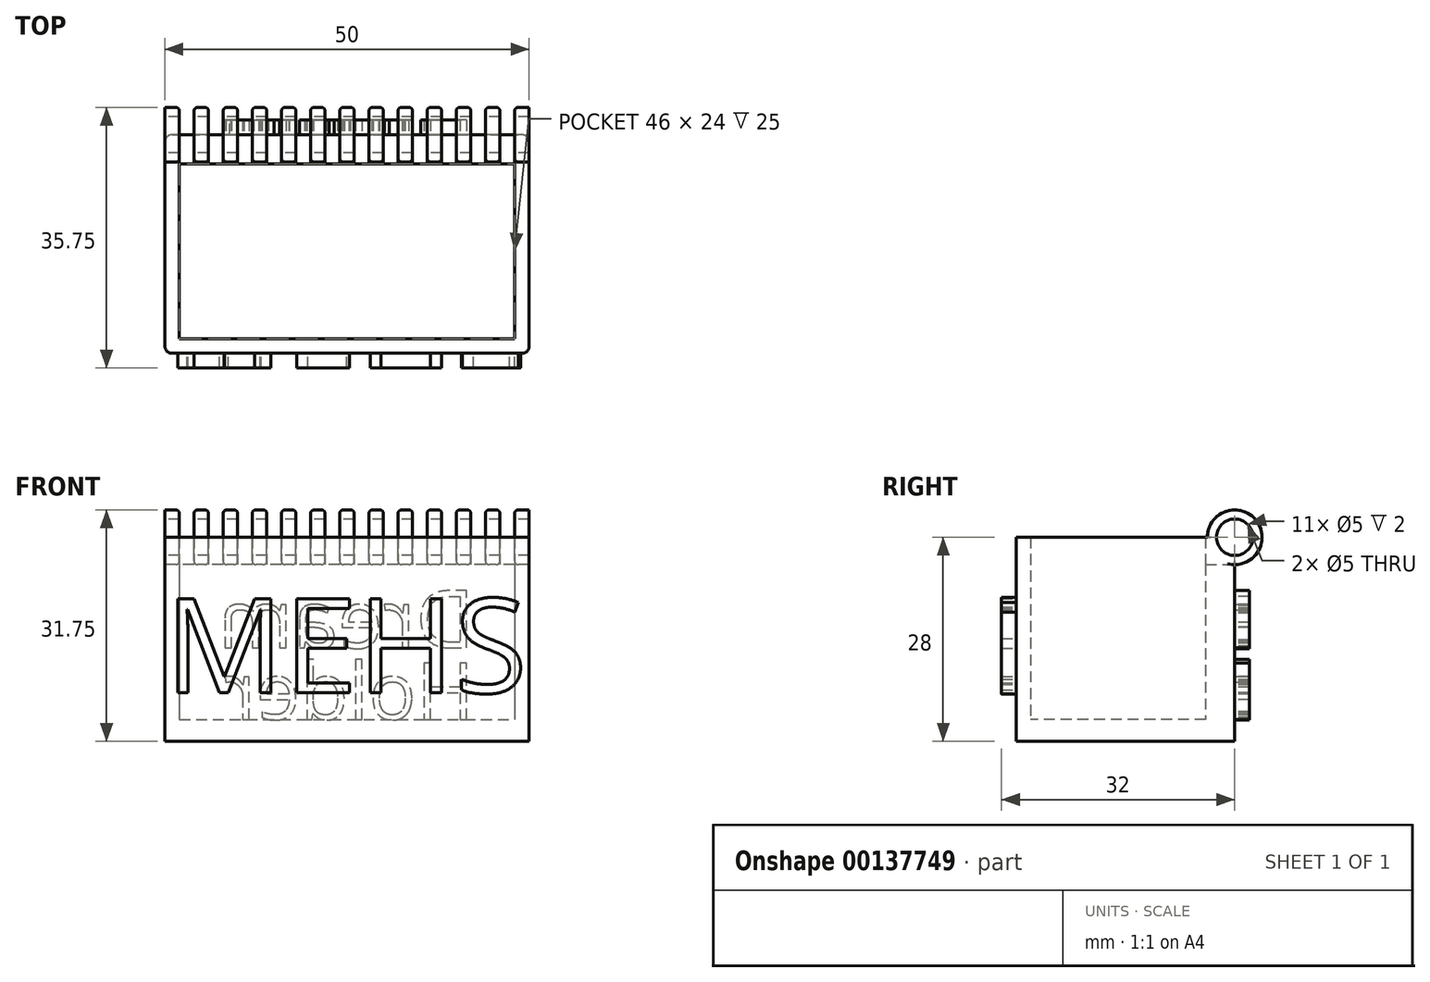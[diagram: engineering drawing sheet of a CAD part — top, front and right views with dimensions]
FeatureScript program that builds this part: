
annotation { "Feature Type Name" : "Feature", "Feature Type Description" : "" }
export const myFeature = defineFeature(function(context is Context, id is Id, definition is map)
    precondition{}
    {
        {
            var Q0;
            Q0=qCreatedBy(makeId("Top.planeOp"),FACE);
            var sketch = newSketch(context, id + "F0", { "sketchPlane" : qUnion([Q0])});
            skLineSegment(sketch, "E0.bottom", {"start": v(-25, 15) * mm, "end": v(25, 15) * mm});
            skLineSegment(sketch, "E0.top", {"start": v(-25, -15) * mm, "end": v(25, -15) * mm});
            skLineSegment(sketch, "E0.left", {"start": v(-25, 15) * mm, "end": v(-25, -15) * mm});
            skLineSegment(sketch, "E0.right", {"start": v(25, 15) * mm, "end": v(25, -15) * mm});
            skSolve(sketch);
        }
        {
            var Q0;
            Q0 = qSketchRegion(id + "F0", true);
            extrude(context, id + "F1", {"entities" : qUnion([Q0]), "depth" : 3 * mm});
        }
        {
            var Q0;
            Q0=makeQuery(id+"F1.opExtrude","CAP_FACE",FACE,{"disambiguationData":[OSD([sQuery(id+"F0.wireOp",EDGE,"E0.bottom"),sQuery(id+"F0.wireOp",EDGE,"E0.top"),sQuery(id+"F0.wireOp",EDGE,"E0.left"),sQuery(id+"F0.wireOp",EDGE,"E0.right")])],"isStart":false});
            var sketch = newSketch(context, id + "F2", { "sketchPlane" : qUnion([Q0])});
            skLineSegment(sketch, "E1.bottom", {"start": v(-25, 15) * mm, "end": v(25, 15) * mm});
            skLineSegment(sketch, "E1.top", {"start": v(-25, -15) * mm, "end": v(25, -15) * mm});
            skLineSegment(sketch, "E1.left", {"start": v(-25, 15) * mm, "end": v(-25, -15) * mm});
            skLineSegment(sketch, "E1.right", {"start": v(25, 15) * mm, "end": v(25, -15) * mm});
            skLineSegment(sketch, "E2.bottom", {"start": v(-23, 11) * mm, "end": v(23, 11) * mm});
            skLineSegment(sketch, "E2.top", {"start": v(-23, -13) * mm, "end": v(23, -13) * mm});
            skLineSegment(sketch, "E2.left", {"start": v(-23, 11) * mm, "end": v(-23, -13) * mm});
            skLineSegment(sketch, "E2.right", {"start": v(23, 11) * mm, "end": v(23, -13) * mm});
            skSolve(sketch);
        }
        {
            var Q0;
            Q0 = qSketchRegion(id + "F2", true);
            extrude(context, id + "F3", {"entities" : qUnion([Q0]), "operationType" : NewBodyOperationType.ADD, "depth" : 25 * mm});
        }
        {
            var Q0;
            Q0=makeQuery(id+"F3.boolean.opBoolean","MERGE",FACE,{"derivedFrom":[makeQuery(id+"F1.opExtrude","SWEPT_FACE",FACE,{"disambiguationData":[OSD([sQuery(id+"F0.wireOp",EDGE,"E0.left")])]}),makeQuery(id+"F3.opExtrude","SWEPT_FACE",FACE,{"disambiguationData":[OSD([sQuery(id+"F2.wireOp",EDGE,"E1.left")])]})]});
            var sketch = newSketch(context, id + "F4", { "sketchPlane" : qUnion([Q0])});
            skCircle(sketch, "E3", {"center": v(-15, 28) * mm, "radius": 2.5 * mm});
            skCircle(sketch, "E4", {"center": v(-15, 28) * mm, "radius": 3.75 * mm});
            skSolve(sketch);
        }
        {
            var Q0;
            Q0 = qSketchRegion(id + "F4", true);
            var Q1;
            Q1=makeQuery(id+"F3.boolean.opBoolean","MERGE",FACE,{"derivedFrom":[makeQuery(id+"F1.opExtrude","SWEPT_FACE",FACE,{"disambiguationData":[OSD([sQuery(id+"F0.wireOp",EDGE,"E0.right")])]}),makeQuery(id+"F3.opExtrude","SWEPT_FACE",FACE,{"disambiguationData":[OSD([sQuery(id+"F2.wireOp",EDGE,"E1.right")])]})]});
            extrude(context, id + "F5", {"entities" : qUnion([Q0]), "operationType" : NewBodyOperationType.ADD, "endBound" : BoundingType.UP_TO_SURFACE, "oppositeDirection" : true, "endBoundEntityFace" : qUnion([Q1]), "depth" : 25 * mm});
        }
        {
            var Q0;
            Q0=makeQuery(id+"F5.boolean.opBoolean","MERGE",FACE,{"derivedFrom":[makeQuery(id+"F3.boolean.opBoolean","MERGE",FACE,{"derivedFrom":[makeQuery(id+"F1.opExtrude","SWEPT_FACE",FACE,{"disambiguationData":[OSD([sQuery(id+"F0.wireOp",EDGE,"E0.right")])]}),makeQuery(id+"F3.opExtrude","SWEPT_FACE",FACE,{"disambiguationData":[OSD([sQuery(id+"F2.wireOp",EDGE,"E1.right")])]})]}),makeQuery(id+"F5.opExtrude","CAP_FACE",FACE,{"disambiguationData":[OSD([sQuery(id+"F4.wireOp",EDGE,"E3"),sQuery(id+"F4.wireOp",EDGE,"E4")])],"isStart":false})]});
            var sketch = newSketch(context, id + "F6", { "sketchPlane" : qUnion([Q0])});
            skCircle(sketch, "E5", {"center": v(15, 28) * mm, "radius": 2.5 * mm});
            skSolve(sketch);
        }
        {
            var Q0;
            Q0 = qSketchRegion(id + "F6", true);
            extrude(context, id + "F7", {"entities" : qUnion([Q0]), "operationType" : NewBodyOperationType.REMOVE, "endBound" : BoundingType.THROUGH_ALL, "oppositeDirection" : true, "depth" : 25 * mm});
        }
        {
            var Q0;
            Q0=qCreatedBy(makeId("Front.planeOp"),FACE);
            cPlane(context, id + "F8", {"entities" : qUnion([Q0]), "cplaneType" : CPlaneType.OFFSET, "offset" : 19 * mm, "oppositeDirection" : true, "width" : 150 * mm, "height" : 150 * mm});
        }
        {
            var Q0;
            Q0=qCreatedBy(id+"F8.planeOp",FACE);
            var sketch = newSketch(context, id + "F9", { "sketchPlane" : qUnion([Q0])});
            skLineSegment(sketch, "E6.bottom", {"start": v(23, 31.75) * mm, "end": v(21, 31.75) * mm});
            skLineSegment(sketch, "E6.top", {"start": v(23, 24.25) * mm, "end": v(21, 24.25) * mm});
            skLineSegment(sketch, "E6.left", {"start": v(23, 31.75) * mm, "end": v(23, 24.25) * mm});
            skLineSegment(sketch, "E6.right", {"start": v(21, 31.75) * mm, "end": v(21, 24.25) * mm});
            skLineSegment(sketch, "E7.1.0.0", {"start": v(17, 31.75) * mm, "end": v(17, 24.25) * mm});
            skLineSegment(sketch, "E7.1.0.1", {"start": v(19, 31.75) * mm, "end": v(17, 31.75) * mm});
            skLineSegment(sketch, "E7.1.0.2", {"start": v(19, 24.25) * mm, "end": v(17, 24.25) * mm});
            skLineSegment(sketch, "E7.1.0.3", {"start": v(19, 31.75) * mm, "end": v(19, 24.25) * mm});
            skLineSegment(sketch, "E7.2.0.0", {"start": v(13, 31.75) * mm, "end": v(13, 24.25) * mm});
            skLineSegment(sketch, "E7.2.0.1", {"start": v(15, 31.75) * mm, "end": v(13, 31.75) * mm});
            skLineSegment(sketch, "E7.2.0.2", {"start": v(15, 24.25) * mm, "end": v(13, 24.25) * mm});
            skLineSegment(sketch, "E7.2.0.3", {"start": v(15, 31.75) * mm, "end": v(15, 24.25) * mm});
            skLineSegment(sketch, "E7.3.0.0", {"start": v(9, 31.75) * mm, "end": v(9, 24.25) * mm});
            skLineSegment(sketch, "E7.3.0.1", {"start": v(11, 31.75) * mm, "end": v(9, 31.75) * mm});
            skLineSegment(sketch, "E7.3.0.2", {"start": v(11, 24.25) * mm, "end": v(9, 24.25) * mm});
            skLineSegment(sketch, "E7.3.0.3", {"start": v(11, 31.75) * mm, "end": v(11, 24.25) * mm});
            skLineSegment(sketch, "E7.4.0.0", {"start": v(5, 31.75) * mm, "end": v(5, 24.25) * mm});
            skLineSegment(sketch, "E7.4.0.1", {"start": v(7, 31.75) * mm, "end": v(5, 31.75) * mm});
            skLineSegment(sketch, "E7.4.0.2", {"start": v(7, 24.25) * mm, "end": v(5, 24.25) * mm});
            skLineSegment(sketch, "E7.4.0.3", {"start": v(7, 31.75) * mm, "end": v(7, 24.25) * mm});
            skLineSegment(sketch, "E7.5.0.0", {"start": v(1, 31.75) * mm, "end": v(1, 24.25) * mm});
            skLineSegment(sketch, "E7.5.0.1", {"start": v(3, 31.75) * mm, "end": v(1, 31.75) * mm});
            skLineSegment(sketch, "E7.5.0.2", {"start": v(3, 24.25) * mm, "end": v(1, 24.25) * mm});
            skLineSegment(sketch, "E7.5.0.3", {"start": v(3, 31.75) * mm, "end": v(3, 24.25) * mm});
            skLineSegment(sketch, "E7.6.0.0", {"start": v(-3, 31.75) * mm, "end": v(-3, 24.25) * mm});
            skLineSegment(sketch, "E7.6.0.1", {"start": v(-1, 31.75) * mm, "end": v(-3, 31.75) * mm});
            skLineSegment(sketch, "E7.6.0.2", {"start": v(-1, 24.25) * mm, "end": v(-3, 24.25) * mm});
            skLineSegment(sketch, "E7.6.0.3", {"start": v(-1, 31.75) * mm, "end": v(-1, 24.25) * mm});
            skLineSegment(sketch, "E7.7.0.0", {"start": v(-7, 31.75) * mm, "end": v(-7, 24.25) * mm});
            skLineSegment(sketch, "E7.7.0.1", {"start": v(-5, 31.75) * mm, "end": v(-7, 31.75) * mm});
            skLineSegment(sketch, "E7.7.0.2", {"start": v(-5, 24.25) * mm, "end": v(-7, 24.25) * mm});
            skLineSegment(sketch, "E7.7.0.3", {"start": v(-5, 31.75) * mm, "end": v(-5, 24.25) * mm});
            skLineSegment(sketch, "E7.8.0.0", {"start": v(-11, 31.75) * mm, "end": v(-11, 24.25) * mm});
            skLineSegment(sketch, "E7.8.0.1", {"start": v(-9, 31.75) * mm, "end": v(-11, 31.75) * mm});
            skLineSegment(sketch, "E7.8.0.2", {"start": v(-9, 24.25) * mm, "end": v(-11, 24.25) * mm});
            skLineSegment(sketch, "E7.8.0.3", {"start": v(-9, 31.75) * mm, "end": v(-9, 24.25) * mm});
            skLineSegment(sketch, "E7.9.0.0", {"start": v(-15, 31.75) * mm, "end": v(-15, 24.25) * mm});
            skLineSegment(sketch, "E7.9.0.1", {"start": v(-13, 31.75) * mm, "end": v(-15, 31.75) * mm});
            skLineSegment(sketch, "E7.9.0.2", {"start": v(-13, 24.25) * mm, "end": v(-15, 24.25) * mm});
            skLineSegment(sketch, "E7.9.0.3", {"start": v(-13, 31.75) * mm, "end": v(-13, 24.25) * mm});
            skLineSegment(sketch, "E7.10.0.0", {"start": v(-19, 31.75) * mm, "end": v(-19, 24.25) * mm});
            skLineSegment(sketch, "E7.10.0.1", {"start": v(-17, 31.75) * mm, "end": v(-19, 31.75) * mm});
            skLineSegment(sketch, "E7.10.0.2", {"start": v(-17, 24.25) * mm, "end": v(-19, 24.25) * mm});
            skLineSegment(sketch, "E7.10.0.3", {"start": v(-17, 31.75) * mm, "end": v(-17, 24.25) * mm});
            skLineSegment(sketch, "E7.11.0.0", {"start": v(-23, 31.75) * mm, "end": v(-23, 24.25) * mm});
            skLineSegment(sketch, "E7.11.0.1", {"start": v(-21, 31.75) * mm, "end": v(-23, 31.75) * mm});
            skLineSegment(sketch, "E7.11.0.2", {"start": v(-21, 24.25) * mm, "end": v(-23, 24.25) * mm});
            skLineSegment(sketch, "E7.11.0.3", {"start": v(-21, 31.75) * mm, "end": v(-21, 24.25) * mm});
            skLineSegment(sketch, "E7.direction1", {"start": v(21, 24.25) * mm, "end": v(17, 24.25) * mm, "construction": true});
            skSolve(sketch);
        }
        {
            var Q0;
            Q0 = qSketchRegion(id + "F9", true);
            extrude(context, id + "F10", {"entities" : qUnion([Q0]), "operationType" : NewBodyOperationType.REMOVE, "depth" : 10 * mm});
        }
        {
            var Q0;
            Q0=makeQuery(id+"F3.boolean.opBoolean","MERGE",FACE,{"derivedFrom":[makeQuery(id+"F1.opExtrude","SWEPT_FACE",FACE,{"disambiguationData":[OSD([sQuery(id+"F0.wireOp",EDGE,"E0.top")])]}),makeQuery(id+"F3.opExtrude","SWEPT_FACE",FACE,{"disambiguationData":[OSD([sQuery(id+"F2.wireOp",EDGE,"E1.top")])]})]});
            var sketch = newSketch(context, id + "F11", { "sketchPlane" : qUnion([Q0])});
            skText(sketch, "E8", { "text": "MEHS", "fontName": "OpenSans-Regular.ttf"});
            const initialGuessF11  = {"E8": [-0.025, 0.00665, 1, 0, 0.01303]};
            skSetInitialGuess(sketch, initialGuessF11);
            skSolve(sketch);
        }
        {
            var Q0;
            Q0 = qSketchRegion(id + "F11", true);
            extrude(context, id + "F12", {"entities" : qUnion([Q0]), "operationType" : NewBodyOperationType.ADD, "depth" : 2 * mm});
        }
        {
            var Q0;
            {var subQ2=sQuery(id+"F0.wireOp",EDGE,"E0.bottom");var subQ3=sQuery(id+"F4.wireOp",EDGE,"E4");Q0=makeQuery(id+"F5.boolean.opBoolean","SPLIT",FACE,{"disambiguationData":[TD([makeQuery(id+"F5.opExtrude","SWEPT_FACE",FACE,{"disambiguationData":[OSD([subQ3])]})])],"derivedFrom":makeQuery(id+"F3.boolean.opBoolean","MERGE",FACE,{"derivedFrom":[makeQuery(id+"F1.opExtrude","SWEPT_FACE",FACE,{"disambiguationData":[OSD([subQ2])]}),makeQuery(id+"F3.opExtrude","SWEPT_FACE",FACE,{"disambiguationData":[OSD([sQuery(id+"F2.wireOp",EDGE,"E1.bottom")])]})]})});}
            var sketch = newSketch(context, id + "F13", { "sketchPlane" : qUnion([Q0])});
            skText(sketch, "E9", { "text": "Dream", "fontName": "OpenSans-Regular.ttf"});
            skText(sketch, "E10", { "text": "Holder", "fontName": "OpenSans-Regular.ttf"});
            const initialGuessF13  = {"E9": [-0.0175, 0.0128, 1, 0, 0.00795], "E10": [-0.0175, 0.003, 1, 0, 0.0078]};
            skSetInitialGuess(sketch, initialGuessF13);
            skSolve(sketch);
        }
        {
            var Q0;
            Q0 = qSketchRegion(id + "F13", true);
            extrude(context, id + "F14", {"entities" : qUnion([Q0]), "operationType" : NewBodyOperationType.ADD, "depth" : 2 * mm});
        }
        {
            var Q0;
            {var subQ0=sQuery(id+"F2.wireOp",EDGE,"E1.bottom");var subQ1=sQuery(id+"F0.wireOp",EDGE,"E0.left");var subQ2=sQuery(id+"F0.wireOp",EDGE,"E0.bottom");var subQ3=sQuery(id+"F2.wireOp",EDGE,"E1.left");var subQ4=sQuery(id+"F4.wireOp",EDGE,"E4");Q0=makeQuery(id+"F5.boolean.opBoolean","SPLIT",EDGE,{"disambiguationData":[TD([makeQuery(id+"F5.opExtrude","SWEPT_FACE",FACE,{"disambiguationData":[OSD([subQ4])]})])],"derivedFrom":makeQuery(id+"F3.boolean.opBoolean","MERGE",EDGE,{"derivedFrom":[makeQuery(id+"F1.opExtrude","SWEPT_EDGE",EDGE,{"disambiguationData":[OSD([subQ2,subQ1])]}),makeQuery(id+"F3.opExtrude","SWEPT_EDGE",EDGE,{"disambiguationData":[OSD([subQ0,subQ3])]})]})});}
            var Q1;
            Q1=makeQuery(id+"F3.boolean.opBoolean","MERGE",EDGE,{"derivedFrom":[makeQuery(id+"F1.opExtrude","SWEPT_EDGE",EDGE,{"disambiguationData":[OSD([sQuery(id+"F0.wireOp",EDGE,"E0.top"),sQuery(id+"F0.wireOp",EDGE,"E0.left")])]}),makeQuery(id+"F3.opExtrude","SWEPT_EDGE",EDGE,{"disambiguationData":[OSD([sQuery(id+"F2.wireOp",EDGE,"E1.top"),sQuery(id+"F2.wireOp",EDGE,"E1.left")])]})]});
            var Q2;
            Q2=makeQuery(id+"F3.boolean.opBoolean","MERGE",EDGE,{"derivedFrom":[makeQuery(id+"F1.opExtrude","SWEPT_EDGE",EDGE,{"disambiguationData":[OSD([sQuery(id+"F0.wireOp",EDGE,"E0.top"),sQuery(id+"F0.wireOp",EDGE,"E0.right")])]}),makeQuery(id+"F3.opExtrude","SWEPT_EDGE",EDGE,{"disambiguationData":[OSD([sQuery(id+"F2.wireOp",EDGE,"E1.top"),sQuery(id+"F2.wireOp",EDGE,"E1.right")])]})]});
            var Q3;
            {var subQ0=sQuery(id+"F2.wireOp",EDGE,"E1.bottom");var subQ1=sQuery(id+"F0.wireOp",EDGE,"E0.right");var subQ2=sQuery(id+"F0.wireOp",EDGE,"E0.bottom");var subQ3=sQuery(id+"F2.wireOp",EDGE,"E1.right");var subQ4=sQuery(id+"F4.wireOp",EDGE,"E4");Q3=makeQuery(id+"F5.boolean.opBoolean","SPLIT",EDGE,{"disambiguationData":[TD([makeQuery(id+"F5.opExtrude","SWEPT_FACE",FACE,{"disambiguationData":[OSD([subQ4])]})])],"derivedFrom":makeQuery(id+"F3.boolean.opBoolean","MERGE",EDGE,{"derivedFrom":[makeQuery(id+"F1.opExtrude","SWEPT_EDGE",EDGE,{"disambiguationData":[OSD([subQ2,subQ1])]}),makeQuery(id+"F3.opExtrude","SWEPT_EDGE",EDGE,{"disambiguationData":[OSD([subQ0,subQ3])]})]})});}
            fillet(context, id + "F15", {"entities" : qUnion([Q0, Q1, Q2, Q3]), "radius" : 1 * mm, "tangentPropagation" : true, "allowEdgeOverflow" : false});
        }
        {
            var Q0;
            Q0=makeQuery(id+"F10.boolean.opBoolean","INTERSECT",EDGE,{"derivedFrom":[makeQuery(id+"F5.opExtrude","SWEPT_FACE",FACE,{"disambiguationData":[OSD([sQuery(id+"F4.wireOp",EDGE,"E4")])]}),makeQuery(id+"F10.opExtrude","SWEPT_FACE",FACE,{"disambiguationData":[OSD([sQuery(id+"F9.wireOp",EDGE,"E6.left")])]})]});
            var Q1;
            Q1=makeQuery(id+"F10.boolean.opBoolean","INTERSECT",EDGE,{"derivedFrom":[makeQuery(id+"F5.opExtrude","SWEPT_FACE",FACE,{"disambiguationData":[OSD([sQuery(id+"F4.wireOp",EDGE,"E4")])]}),makeQuery(id+"F10.opExtrude","SWEPT_FACE",FACE,{"disambiguationData":[OSD([sQuery(id+"F9.wireOp",EDGE,"E6.right")])]})]});
            var Q2;
            Q2=makeQuery(id+"F10.boolean.opBoolean","INTERSECT",EDGE,{"derivedFrom":[makeQuery(id+"F5.opExtrude","SWEPT_FACE",FACE,{"disambiguationData":[OSD([sQuery(id+"F4.wireOp",EDGE,"E4")])]}),makeQuery(id+"F10.opExtrude","SWEPT_FACE",FACE,{"disambiguationData":[OSD([sQuery(id+"F9.wireOp",EDGE,"E7.1.0.3")])]})]});
            var Q3;
            Q3=makeQuery(id+"F10.boolean.opBoolean","INTERSECT",EDGE,{"derivedFrom":[makeQuery(id+"F5.opExtrude","SWEPT_FACE",FACE,{"disambiguationData":[OSD([sQuery(id+"F4.wireOp",EDGE,"E4")])]}),makeQuery(id+"F10.opExtrude","SWEPT_FACE",FACE,{"disambiguationData":[OSD([sQuery(id+"F9.wireOp",EDGE,"E7.1.0.0")])]})]});
            var Q4;
            Q4=makeQuery(id+"F10.boolean.opBoolean","INTERSECT",EDGE,{"derivedFrom":[makeQuery(id+"F5.opExtrude","SWEPT_FACE",FACE,{"disambiguationData":[OSD([sQuery(id+"F4.wireOp",EDGE,"E4")])]}),makeQuery(id+"F10.opExtrude","SWEPT_FACE",FACE,{"disambiguationData":[OSD([sQuery(id+"F9.wireOp",EDGE,"E7.2.0.3")])]})]});
            var Q5;
            Q5=makeQuery(id+"F10.boolean.opBoolean","INTERSECT",EDGE,{"derivedFrom":[makeQuery(id+"F5.opExtrude","SWEPT_FACE",FACE,{"disambiguationData":[OSD([sQuery(id+"F4.wireOp",EDGE,"E4")])]}),makeQuery(id+"F10.opExtrude","SWEPT_FACE",FACE,{"disambiguationData":[OSD([sQuery(id+"F9.wireOp",EDGE,"E7.2.0.0")])]})]});
            var Q6;
            Q6=makeQuery(id+"F10.boolean.opBoolean","INTERSECT",EDGE,{"derivedFrom":[makeQuery(id+"F5.opExtrude","SWEPT_FACE",FACE,{"disambiguationData":[OSD([sQuery(id+"F4.wireOp",EDGE,"E4")])]}),makeQuery(id+"F10.opExtrude","SWEPT_FACE",FACE,{"disambiguationData":[OSD([sQuery(id+"F9.wireOp",EDGE,"E7.3.0.3")])]})]});
            var Q7;
            Q7=makeQuery(id+"F10.boolean.opBoolean","INTERSECT",EDGE,{"derivedFrom":[makeQuery(id+"F5.opExtrude","SWEPT_FACE",FACE,{"disambiguationData":[OSD([sQuery(id+"F4.wireOp",EDGE,"E4")])]}),makeQuery(id+"F10.opExtrude","SWEPT_FACE",FACE,{"disambiguationData":[OSD([sQuery(id+"F9.wireOp",EDGE,"E7.3.0.0")])]})]});
            var Q8;
            Q8=makeQuery(id+"F10.boolean.opBoolean","INTERSECT",EDGE,{"derivedFrom":[makeQuery(id+"F5.opExtrude","SWEPT_FACE",FACE,{"disambiguationData":[OSD([sQuery(id+"F4.wireOp",EDGE,"E4")])]}),makeQuery(id+"F10.opExtrude","SWEPT_FACE",FACE,{"disambiguationData":[OSD([sQuery(id+"F9.wireOp",EDGE,"E7.4.0.3")])]})]});
            var Q9;
            Q9=makeQuery(id+"F10.boolean.opBoolean","INTERSECT",EDGE,{"derivedFrom":[makeQuery(id+"F5.opExtrude","SWEPT_FACE",FACE,{"disambiguationData":[OSD([sQuery(id+"F4.wireOp",EDGE,"E4")])]}),makeQuery(id+"F10.opExtrude","SWEPT_FACE",FACE,{"disambiguationData":[OSD([sQuery(id+"F9.wireOp",EDGE,"E7.4.0.0")])]})]});
            var Q10;
            Q10=makeQuery(id+"F10.boolean.opBoolean","INTERSECT",EDGE,{"derivedFrom":[makeQuery(id+"F5.opExtrude","SWEPT_FACE",FACE,{"disambiguationData":[OSD([sQuery(id+"F4.wireOp",EDGE,"E4")])]}),makeQuery(id+"F10.opExtrude","SWEPT_FACE",FACE,{"disambiguationData":[OSD([sQuery(id+"F9.wireOp",EDGE,"E7.5.0.3")])]})]});
            var Q11;
            Q11=makeQuery(id+"F10.boolean.opBoolean","INTERSECT",EDGE,{"derivedFrom":[makeQuery(id+"F5.opExtrude","SWEPT_FACE",FACE,{"disambiguationData":[OSD([sQuery(id+"F4.wireOp",EDGE,"E4")])]}),makeQuery(id+"F10.opExtrude","SWEPT_FACE",FACE,{"disambiguationData":[OSD([sQuery(id+"F9.wireOp",EDGE,"E7.5.0.0")])]})]});
            var Q12;
            Q12=makeQuery(id+"F10.boolean.opBoolean","INTERSECT",EDGE,{"derivedFrom":[makeQuery(id+"F5.opExtrude","SWEPT_FACE",FACE,{"disambiguationData":[OSD([sQuery(id+"F4.wireOp",EDGE,"E4")])]}),makeQuery(id+"F10.opExtrude","SWEPT_FACE",FACE,{"disambiguationData":[OSD([sQuery(id+"F9.wireOp",EDGE,"E7.6.0.3")])]})]});
            var Q13;
            Q13=makeQuery(id+"F10.boolean.opBoolean","INTERSECT",EDGE,{"derivedFrom":[makeQuery(id+"F5.opExtrude","SWEPT_FACE",FACE,{"disambiguationData":[OSD([sQuery(id+"F4.wireOp",EDGE,"E4")])]}),makeQuery(id+"F10.opExtrude","SWEPT_FACE",FACE,{"disambiguationData":[OSD([sQuery(id+"F9.wireOp",EDGE,"E7.6.0.0")])]})]});
            var Q14;
            Q14=makeQuery(id+"F10.boolean.opBoolean","INTERSECT",EDGE,{"derivedFrom":[makeQuery(id+"F5.opExtrude","SWEPT_FACE",FACE,{"disambiguationData":[OSD([sQuery(id+"F4.wireOp",EDGE,"E4")])]}),makeQuery(id+"F10.opExtrude","SWEPT_FACE",FACE,{"disambiguationData":[OSD([sQuery(id+"F9.wireOp",EDGE,"E7.7.0.3")])]})]});
            var Q15;
            Q15=makeQuery(id+"F10.boolean.opBoolean","INTERSECT",EDGE,{"derivedFrom":[makeQuery(id+"F5.opExtrude","SWEPT_FACE",FACE,{"disambiguationData":[OSD([sQuery(id+"F4.wireOp",EDGE,"E4")])]}),makeQuery(id+"F10.opExtrude","SWEPT_FACE",FACE,{"disambiguationData":[OSD([sQuery(id+"F9.wireOp",EDGE,"E7.7.0.0")])]})]});
            var Q16;
            Q16=makeQuery(id+"F10.boolean.opBoolean","INTERSECT",EDGE,{"derivedFrom":[makeQuery(id+"F5.opExtrude","SWEPT_FACE",FACE,{"disambiguationData":[OSD([sQuery(id+"F4.wireOp",EDGE,"E4")])]}),makeQuery(id+"F10.opExtrude","SWEPT_FACE",FACE,{"disambiguationData":[OSD([sQuery(id+"F9.wireOp",EDGE,"E7.8.0.3")])]})]});
            var Q17;
            Q17=makeQuery(id+"F10.boolean.opBoolean","INTERSECT",EDGE,{"derivedFrom":[makeQuery(id+"F5.opExtrude","SWEPT_FACE",FACE,{"disambiguationData":[OSD([sQuery(id+"F4.wireOp",EDGE,"E4")])]}),makeQuery(id+"F10.opExtrude","SWEPT_FACE",FACE,{"disambiguationData":[OSD([sQuery(id+"F9.wireOp",EDGE,"E7.8.0.0")])]})]});
            var Q18;
            Q18=makeQuery(id+"F10.boolean.opBoolean","INTERSECT",EDGE,{"derivedFrom":[makeQuery(id+"F5.opExtrude","SWEPT_FACE",FACE,{"disambiguationData":[OSD([sQuery(id+"F4.wireOp",EDGE,"E4")])]}),makeQuery(id+"F10.opExtrude","SWEPT_FACE",FACE,{"disambiguationData":[OSD([sQuery(id+"F9.wireOp",EDGE,"E7.9.0.3")])]})]});
            var Q19;
            Q19=makeQuery(id+"F10.boolean.opBoolean","INTERSECT",EDGE,{"derivedFrom":[makeQuery(id+"F5.opExtrude","SWEPT_FACE",FACE,{"disambiguationData":[OSD([sQuery(id+"F4.wireOp",EDGE,"E4")])]}),makeQuery(id+"F10.opExtrude","SWEPT_FACE",FACE,{"disambiguationData":[OSD([sQuery(id+"F9.wireOp",EDGE,"E7.9.0.0")])]})]});
            var Q20;
            Q20=makeQuery(id+"F10.boolean.opBoolean","INTERSECT",EDGE,{"derivedFrom":[makeQuery(id+"F5.opExtrude","SWEPT_FACE",FACE,{"disambiguationData":[OSD([sQuery(id+"F4.wireOp",EDGE,"E4")])]}),makeQuery(id+"F10.opExtrude","SWEPT_FACE",FACE,{"disambiguationData":[OSD([sQuery(id+"F9.wireOp",EDGE,"E7.10.0.3")])]})]});
            var Q21;
            Q21=makeQuery(id+"F10.boolean.opBoolean","INTERSECT",EDGE,{"derivedFrom":[makeQuery(id+"F5.opExtrude","SWEPT_FACE",FACE,{"disambiguationData":[OSD([sQuery(id+"F4.wireOp",EDGE,"E4")])]}),makeQuery(id+"F10.opExtrude","SWEPT_FACE",FACE,{"disambiguationData":[OSD([sQuery(id+"F9.wireOp",EDGE,"E7.10.0.0")])]})]});
            var Q22;
            Q22=makeQuery(id+"F10.boolean.opBoolean","INTERSECT",EDGE,{"derivedFrom":[makeQuery(id+"F5.opExtrude","SWEPT_FACE",FACE,{"disambiguationData":[OSD([sQuery(id+"F4.wireOp",EDGE,"E4")])]}),makeQuery(id+"F10.opExtrude","SWEPT_FACE",FACE,{"disambiguationData":[OSD([sQuery(id+"F9.wireOp",EDGE,"E7.11.0.3")])]})]});
            var Q23;
            Q23=makeQuery(id+"F10.boolean.opBoolean","INTERSECT",EDGE,{"derivedFrom":[makeQuery(id+"F5.opExtrude","SWEPT_FACE",FACE,{"disambiguationData":[OSD([sQuery(id+"F4.wireOp",EDGE,"E4")])]}),makeQuery(id+"F10.opExtrude","SWEPT_FACE",FACE,{"disambiguationData":[OSD([sQuery(id+"F9.wireOp",EDGE,"E7.11.0.0")])]})]});
            fillet(context, id + "F16", {"entities" : qUnion([Q0, Q1, Q2, Q3, Q4, Q5, Q6, Q7, Q8, Q9, Q10, Q11, Q12, Q13, Q14, Q15, Q16, Q17, Q18, Q19, Q20, Q21, Q22, Q23]), "radius" : .5 * mm, "tangentPropagation" : true, "allowEdgeOverflow" : false});
        }
    });
